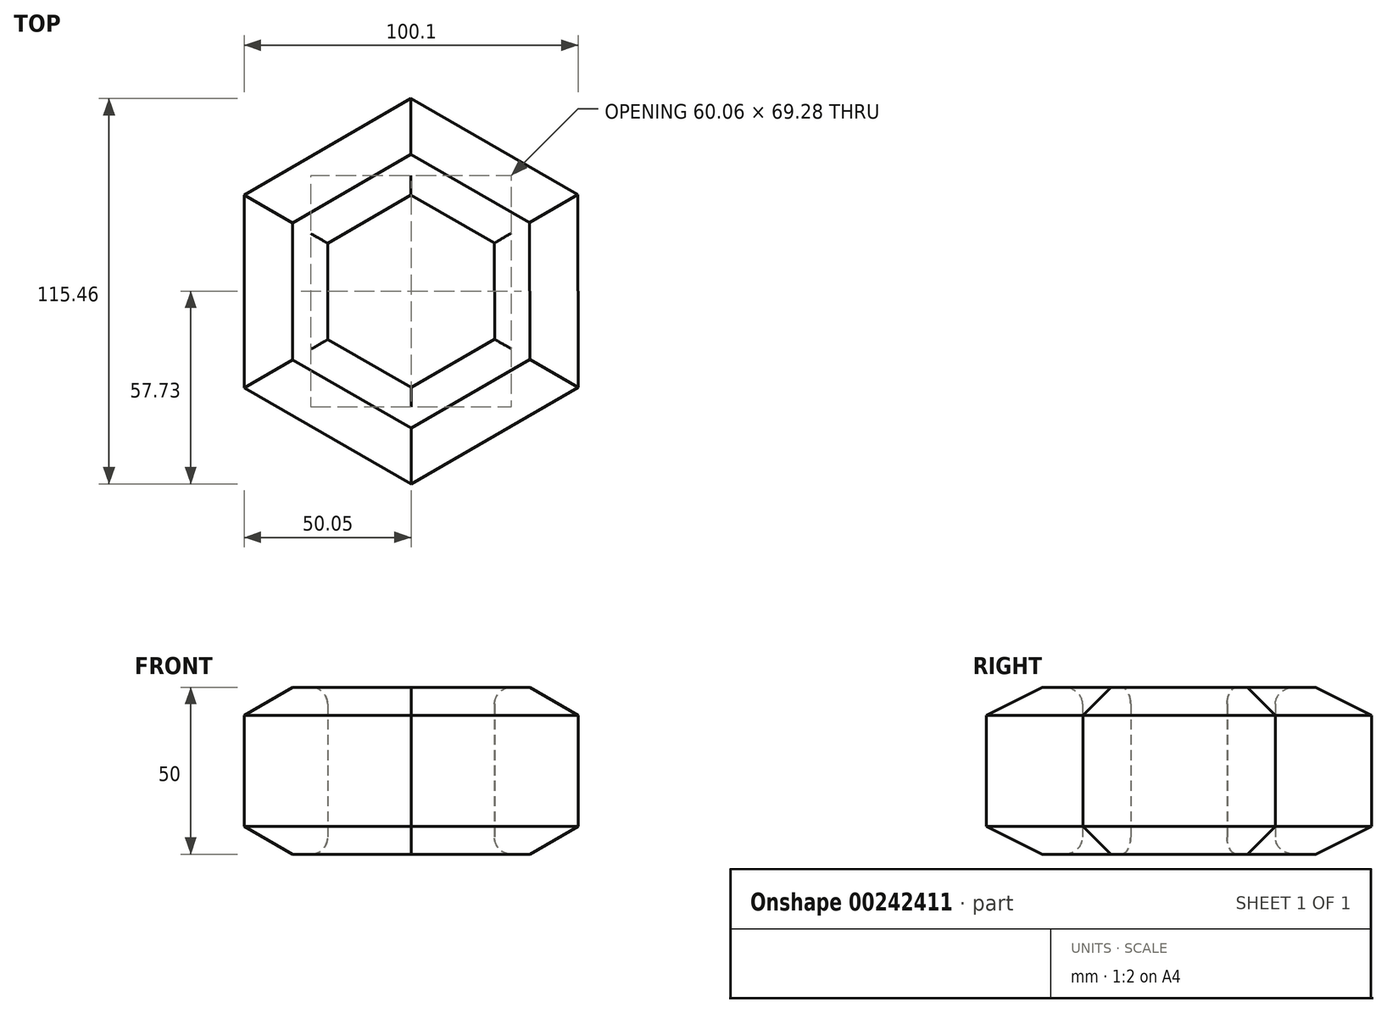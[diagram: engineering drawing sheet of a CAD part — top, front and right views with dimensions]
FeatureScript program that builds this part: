
annotation { "Feature Type Name" : "Feature", "Feature Type Description" : "" }
export const myFeature = defineFeature(function(context is Context, id is Id, definition is map)
    precondition{}
    {
        {
            var Q0;
            Q0=qCreatedBy(makeId("Top.planeOp"),FACE);
            var sketch = newSketch(context, id + "F0", { "sketchPlane" : qUnion([Q0])});
            skCircle(sketch, "E0.cCircle", {"center": v(0, 0) * mm, "radius": 50 * mm, "construction": true});
            skLineSegment(sketch, "E0.0", {"start": v(-50.05, 28.79) * mm, "end": v(-0.1, 57.73) * mm});
            skLineSegment(sketch, "E0.1", {"start": v(-0.1, 57.73) * mm, "end": v(49.95, 28.95) * mm});
            skLineSegment(sketch, "E0.2", {"start": v(49.95, 28.95) * mm, "end": v(50.05, -28.79) * mm});
            skLineSegment(sketch, "E0.3", {"start": v(50.05, -28.79) * mm, "end": v(0.1, -57.73) * mm});
            skLineSegment(sketch, "E0.4", {"start": v(0.1, -57.73) * mm, "end": v(-49.95, -28.95) * mm});
            skLineSegment(sketch, "E0.5", {"start": v(-49.95, -28.95) * mm, "end": v(-50.05, 28.79) * mm});
            skPoint(sketch, "E0.0.midPoint", {"position": v(-25.07, 43.26) * mm});
            skCircle(sketch, "E1", {"center": v(0, 0) * mm, "radius": 25 * mm});
            skSolve(sketch);
        }
        {
            var Q0;
            Q0=qCreatedBy(makeId("Front.planeOp"),FACE);
            var sketch = newSketch(context, id + "F1", { "sketchPlane" : qUnion([Q0])});
            skLineSegment(sketch, "E2", {"start": v(-25, 0) * mm, "end": v(-25, 25) * mm});
            skLineSegment(sketch, "E3", {"start": v(-25, 25) * mm, "end": v(-35.51, 25) * mm});
            skLineSegment(sketch, "E4", {"start": v(-35.51, 25) * mm, "end": v(-50, 16.64) * mm});
            skLineSegment(sketch, "E5", {"start": v(-50, 16.64) * mm, "end": v(-50, 0) * mm});
            skLineSegment(sketch, "E6.MirrorCS", {"start": v(-50, -16.64) * mm, "end": v(-50, 0) * mm});
            skLineSegment(sketch, "E7.MirrorCS", {"start": v(-35.51, -25) * mm, "end": v(-50, -16.64) * mm});
            skLineSegment(sketch, "E8.MirrorCS", {"start": v(-25, -25) * mm, "end": v(-35.51, -25) * mm});
            skLineSegment(sketch, "E9.MirrorCS", {"start": v(-25, 0) * mm, "end": v(-25, -25) * mm});
            skSolve(sketch);
        }
        {
            var Q0;
            Q0=makeQuery(id+"F1.imprint","IMPRINT",FACE,{"disambiguationData":[TD([[makeQuery(id+"F1.imprint","IMPRINT",EDGE,{"derivedFrom":sQuery(id+"F1.wireOp",EDGE,"E2")}),1.0]])]});
            var Q1;
            Q1=sQuery(id+"F0.wireOp",EDGE,"E0.5");
            var Q2;
            Q2=sQuery(id+"F0.wireOp",EDGE,"E0.0");
            var Q3;
            Q3=sQuery(id+"F0.wireOp",EDGE,"E0.1");
            var Q4;
            Q4=sQuery(id+"F0.wireOp",EDGE,"E0.2");
            var Q5;
            Q5=sQuery(id+"F0.wireOp",EDGE,"E0.3");
            var Q6;
            Q6=sQuery(id+"F0.wireOp",EDGE,"E0.4");
            sweep(context, id + "F2", {"profiles" : qUnion([Q0]), "path" : qUnion([Q1, Q2, Q3, Q4, Q5, Q6])});
        }
        {
            var Q0;
            Q0=makeQuery(id+"F2.opSweep","SWEPT_EDGE",EDGE,{"disambiguationData":[OSD([sQuery(id+"F0.wireOp",EDGE,"E0.1"),sQuery(id+"F1.wireOp",EDGE,"E2"),sQuery(id+"F1.wireOp",EDGE,"E3")])]});
            var Q1;
            Q1=makeQuery(id+"F2.opSweep","SWEPT_EDGE",EDGE,{"disambiguationData":[OSD([sQuery(id+"F0.wireOp",EDGE,"E0.2"),sQuery(id+"F1.wireOp",EDGE,"E2"),sQuery(id+"F1.wireOp",EDGE,"E3")])]});
            var Q2;
            Q2=makeQuery(id+"F2.opSweep","SWEPT_EDGE",EDGE,{"disambiguationData":[OSD([sQuery(id+"F0.wireOp",EDGE,"E0.3"),sQuery(id+"F1.wireOp",EDGE,"E2"),sQuery(id+"F1.wireOp",EDGE,"E3")])]});
            var Q3;
            Q3=makeQuery(id+"F2.opSweep","SWEPT_EDGE",EDGE,{"disambiguationData":[OSD([sQuery(id+"F0.wireOp",EDGE,"E0.4"),sQuery(id+"F1.wireOp",EDGE,"E2"),sQuery(id+"F1.wireOp",EDGE,"E3")])]});
            var Q4;
            Q4=makeQuery(id+"F2.opSweep","SWEPT_EDGE",EDGE,{"disambiguationData":[OSD([sQuery(id+"F0.wireOp",EDGE,"E0.5"),sQuery(id+"F1.wireOp",EDGE,"E2"),sQuery(id+"F1.wireOp",EDGE,"E3")])]});
            var Q5;
            Q5=makeQuery(id+"F2.opSweep","SWEPT_EDGE",EDGE,{"disambiguationData":[OSD([sQuery(id+"F0.wireOp",EDGE,"E0.0"),sQuery(id+"F1.wireOp",EDGE,"E2"),sQuery(id+"F1.wireOp",EDGE,"E3")])]});
            var Q6;
            Q6=makeQuery(id+"F2.opSweep","SWEPT_EDGE",EDGE,{"disambiguationData":[OSD([sQuery(id+"F0.wireOp",EDGE,"E0.0"),sQuery(id+"F1.wireOp",EDGE,"E8.MirrorCS"),sQuery(id+"F1.wireOp",EDGE,"E9.MirrorCS")])]});
            var Q7;
            Q7=makeQuery(id+"F2.opSweep","SWEPT_EDGE",EDGE,{"disambiguationData":[OSD([sQuery(id+"F0.wireOp",EDGE,"E0.5"),sQuery(id+"F1.wireOp",EDGE,"E8.MirrorCS"),sQuery(id+"F1.wireOp",EDGE,"E9.MirrorCS")])]});
            var Q8;
            Q8=makeQuery(id+"F2.opSweep","SWEPT_EDGE",EDGE,{"disambiguationData":[OSD([sQuery(id+"F0.wireOp",EDGE,"E0.4"),sQuery(id+"F1.wireOp",EDGE,"E8.MirrorCS"),sQuery(id+"F1.wireOp",EDGE,"E9.MirrorCS")])]});
            var Q9;
            Q9=makeQuery(id+"F2.opSweep","SWEPT_EDGE",EDGE,{"disambiguationData":[OSD([sQuery(id+"F0.wireOp",EDGE,"E0.3"),sQuery(id+"F1.wireOp",EDGE,"E8.MirrorCS"),sQuery(id+"F1.wireOp",EDGE,"E9.MirrorCS")])]});
            var Q10;
            Q10=makeQuery(id+"F2.opSweep","SWEPT_EDGE",EDGE,{"disambiguationData":[OSD([sQuery(id+"F0.wireOp",EDGE,"E0.2"),sQuery(id+"F1.wireOp",EDGE,"E8.MirrorCS"),sQuery(id+"F1.wireOp",EDGE,"E9.MirrorCS")])]});
            var Q11;
            Q11=makeQuery(id+"F2.opSweep","SWEPT_EDGE",EDGE,{"disambiguationData":[OSD([sQuery(id+"F0.wireOp",EDGE,"E0.1"),sQuery(id+"F1.wireOp",EDGE,"E8.MirrorCS"),sQuery(id+"F1.wireOp",EDGE,"E9.MirrorCS")])]});
            fillet(context, id + "F3", {"entities" : qUnion([Q0, Q1, Q2, Q3, Q4, Q5, Q6, Q7, Q8, Q9, Q10, Q11]), "radius" : 5 * mm, "tangentPropagation" : true, "allowEdgeOverflow" : false});
        }
    });
